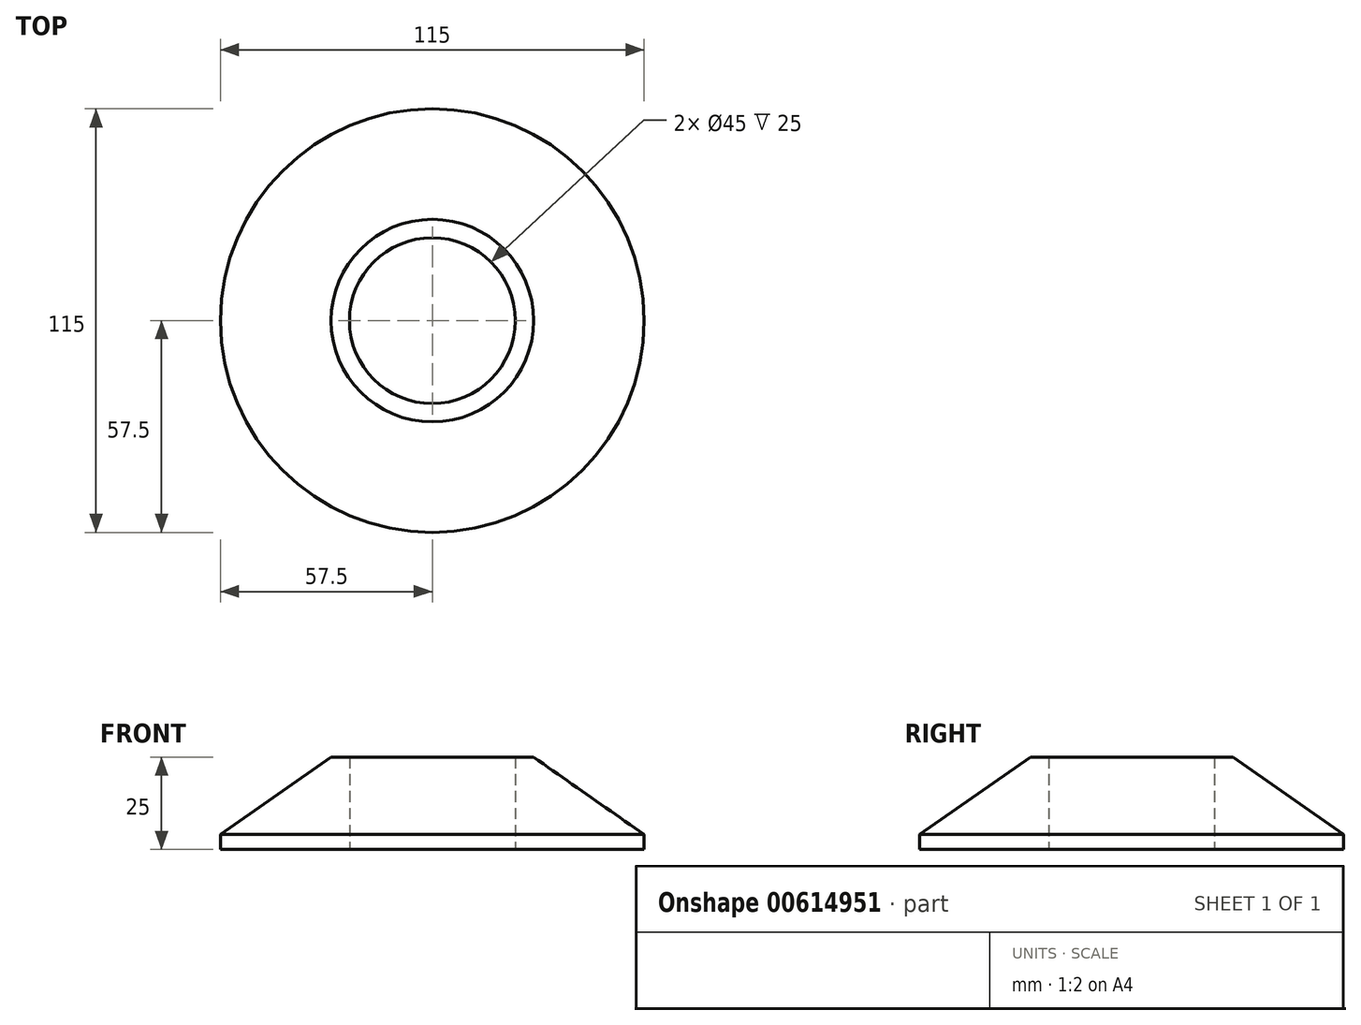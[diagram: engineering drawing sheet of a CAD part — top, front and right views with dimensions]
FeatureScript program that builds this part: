
annotation { "Feature Type Name" : "Feature", "Feature Type Description" : "" }
export const myFeature = defineFeature(function(context is Context, id is Id, definition is map)
    precondition{}
    {
        {
            var Q0;
            Q0=qCreatedBy(makeId("Top.planeOp"),FACE);
            var sketch = newSketch(context, id + "F0", { "sketchPlane" : qUnion([Q0])});
            skCircle(sketch, "E0", {"center": v(0, 0) * mm, "radius": 57.5 * mm});
            skCircle(sketch, "E1", {"center": v(0, 0) * mm, "radius": 25 * mm});
            skCircle(sketch, "E2", {"center": v(0, 0) * mm, "radius": 22.5 * mm});
            skSolve(sketch);
        }
        {
            var Q0;
            Q0=makeQuery(id+"F0.imprint","IMPRINT",FACE,{"disambiguationData":[TD([[makeQuery(id+"F0.imprint","IMPRINT",EDGE,{"derivedFrom":sQuery(id+"F0.wireOp",EDGE,"E0")}),1.0]])]});
            var Q1;
            Q1=qSketchRegion(id+"F0",true);
            var Q2;
            Q2=makeQuery(id+"F0.imprint","IMPRINT",FACE,{"disambiguationData":[TD([[makeQuery(id+"F0.imprint","IMPRINT",EDGE,{"derivedFrom":sQuery(id+"F0.wireOp",EDGE,"E1")}),1.0]])]});
            extrude(context, id + "F1", {"entities" : qUnion([Q0, Q1, Q2]), "depth" : 25 * mm, "offsetDistance" : 25 * mm});
        }
        {
            var Q0;
            Q0=makeQuery(id+"F1.opExtrude","CAP_EDGE",EDGE,{"disambiguationData":[OSD([sQuery(id+"F0.wireOp",EDGE,"E0")])],"isStart":false});
            chamfer(context, id + "F2", {"entities" : qUnion([Q0]), "chamferType" : ChamferType.OFFSET_ANGLE, "width" : 30 * mm, "oppositeDirection" : false, "angle" : 35 * degree, "tangentPropagation" : true});
        }
    });
